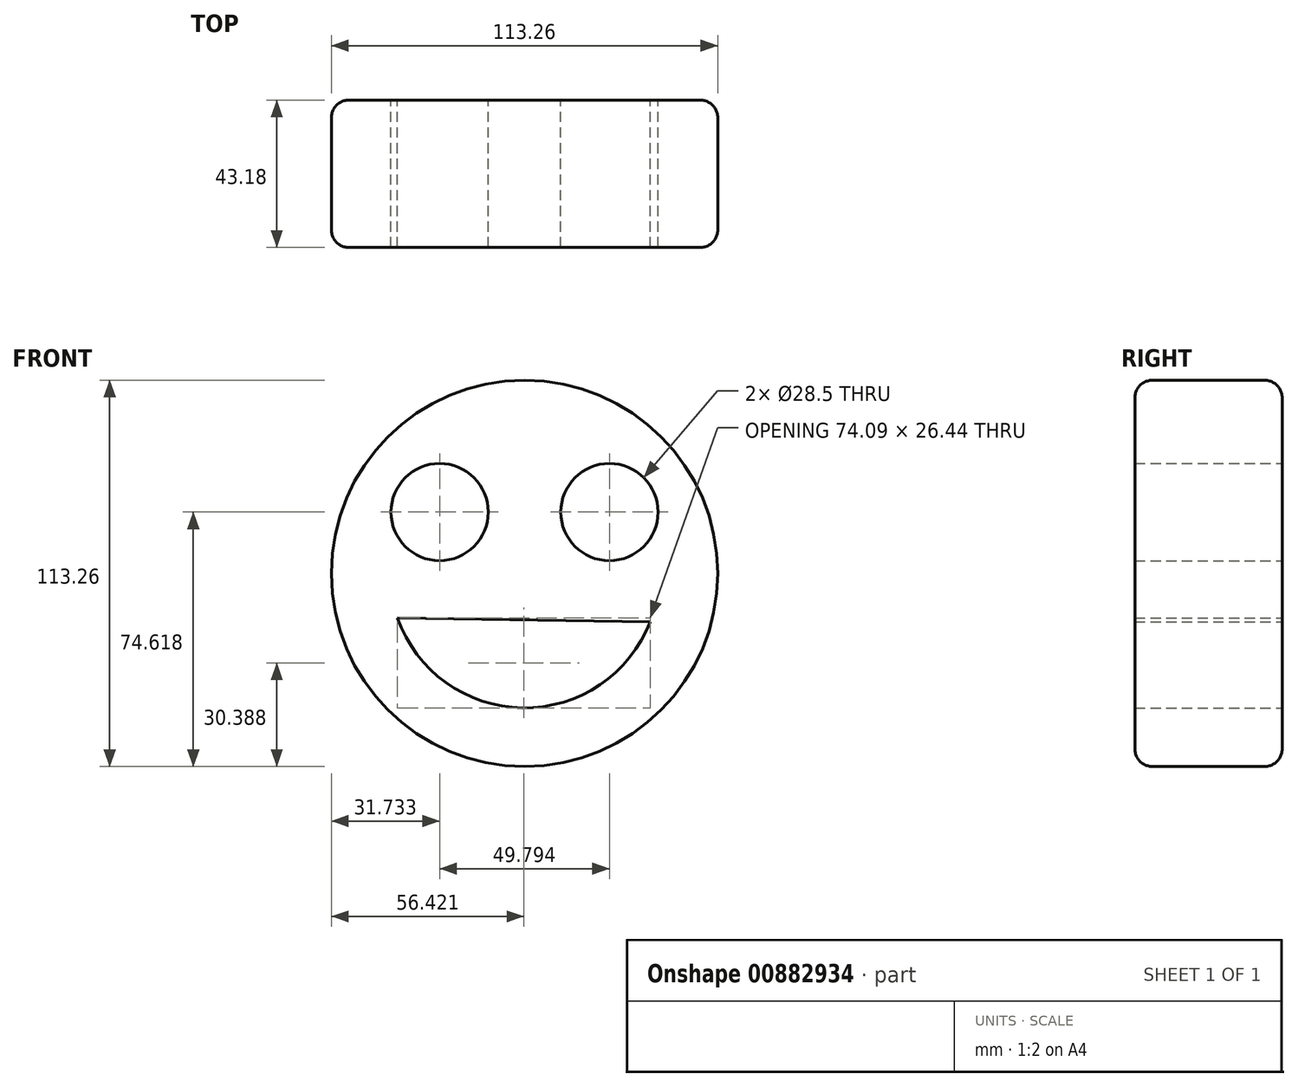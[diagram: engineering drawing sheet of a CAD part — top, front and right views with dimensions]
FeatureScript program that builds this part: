
annotation { "Feature Type Name" : "Feature", "Feature Type Description" : "" }
export const myFeature = defineFeature(function(context is Context, id is Id, definition is map)
    precondition{}
    {
        {
            var Q0;
            Q0=qCreatedBy(makeId("Front.planeOp"),FACE);
            var sketch = newSketch(context, id + "F0", { "sketchPlane" : qUnion([Q0])});
            skCircle(sketch, "E0", {"center": v(0, 0) * mm, "radius": 56.63 * mm});
            skCircle(sketch, "E1", {"center": v(-24.9, 17.99) * mm, "radius": 14.25 * mm});
            skCircle(sketch, "E2.MirrorC", {"center": v(24.9, 17.99) * mm, "radius": 14.25 * mm});
            skArc(sketch, "E3", {"start": v(-37.25, -13.02) * mm, "mid": v(-0.6, -39.46) * mm, "end": v(36.84, -14.16) * mm});
            skLineSegment(sketch, "E4", {"start": v(-37.25, -13.02) * mm, "end": v(36.84, -14.16) * mm});
            skSolve(sketch);
        }
        {
            var Q0;
            Q0=makeQuery(id+"F0.imprint","IMPRINT",FACE,{"disambiguationData":[TD([[makeQuery(id+"F0.imprint","IMPRINT",EDGE,{"derivedFrom":sQuery(id+"F0.wireOp",EDGE,"E0")}),1.0]])]});
            extrude(context, id + "F1", {"entities" : qUnion([Q0]), "depth" : 43.18 * mm, "offsetDistance" : 25.4 * mm});
        }
        {
            var Q0;
            Q0=makeQuery(id+"F1.opExtrude","CAP_EDGE",EDGE,{"disambiguationData":[OSD([sQuery(id+"F0.wireOp",EDGE,"E0")])],"isStart":false});
            var Q1;
            Q1=makeQuery(id+"F1.opExtrude","SWEPT_FACE",FACE,{"disambiguationData":[OSD([sQuery(id+"F0.wireOp",EDGE,"E0")])]});
            fillet(context, id + "F2", {"entities" : qUnion([Q0, Q1]), "radius" : 5.08 * mm, "tangentPropagation" : true, "allowEdgeOverflow" : false});
        }
    });
